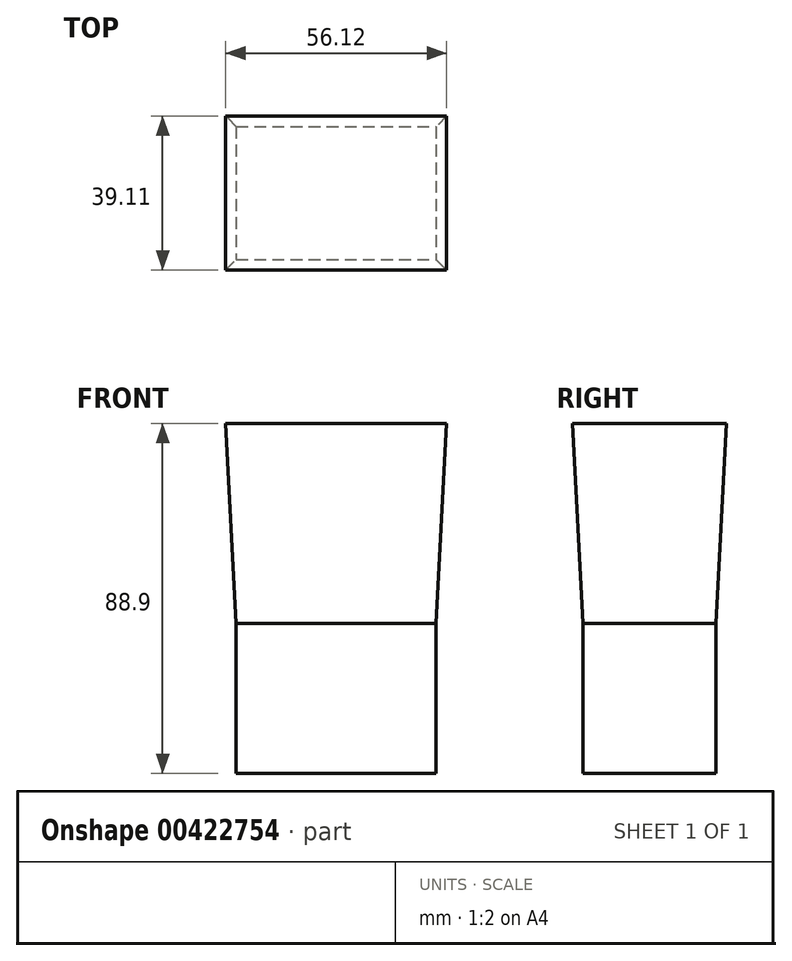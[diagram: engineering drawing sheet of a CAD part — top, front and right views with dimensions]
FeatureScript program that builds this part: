
annotation { "Feature Type Name" : "Feature", "Feature Type Description" : "" }
export const myFeature = defineFeature(function(context is Context, id is Id, definition is map)
    precondition{}
    {
        {
            var Q0;
            Q0=qCreatedBy(makeId("Top.planeOp"),FACE);
            var sketch = newSketch(context, id + "F0", { "sketchPlane" : qUnion([Q0])});
            skLineSegment(sketch, "E0.bottom", {"start": v(-50.8, 51.67) * mm, "end": v(0, 51.67) * mm});
            skLineSegment(sketch, "E0.top", {"start": v(-50.8, 17.9) * mm, "end": v(0, 17.9) * mm});
            skLineSegment(sketch, "E0.left", {"start": v(-50.8, 51.67) * mm, "end": v(-50.8, 17.9) * mm});
            skLineSegment(sketch, "E0.right", {"start": v(0, 51.67) * mm, "end": v(0, 17.9) * mm});
            skSolve(sketch);
        }
        {
            var Q0;
            Q0=makeQuery(id+"F0.imprint","IMPRINT",FACE,{"disambiguationData":[TD([[makeQuery(id+"F0.imprint","IMPRINT",EDGE,{"derivedFrom":sQuery(id+"F0.wireOp",EDGE,"E0.bottom")}),-1.0]])]});
            extrude(context, id + "F1", {"entities" : qUnion([Q0]), "depth" : 50.8 * mm, "offsetDistance" : 25.4 * mm, "hasDraft" : true, "draftAngle" : 3 * degree, "hasSecondDirection" : true, "secondDirectionOppositeDirection" : true, "secondDirectionDepth" : 38.1 * mm});
        }
    });
